# Revit family: WBW_VasteBeglazing 1 vak
name_source: partatom
category: Windows
revit_build: Autodesk Revit Architecture 2013 (Build: 20120221_2030(x64)
units: mm (PartAtom-declared; Revit-internal decimal feet)

## types (1)
- RT element vast beglaasd
    Aanzicht Kader 110mm = No
    Aanzicht Kader 68mm = Yes
    Aanzicht Kader 78mm = No
    Aanzicht Kader 88mm = No
    Aanzicht Tussen Regel 110mm = No
    Aanzicht Tussen Regel 150mm = No
    Aanzicht Tussen Regel 200mm = No
    Aanzicht Tussen Regel 68mm = No
    Aanzicht Tussen Regel 78mm = Yes
    Aanzicht Tussen Regel 88mm = No
    Aanzicht Tussen Stijl 110mm = No
    Aanzicht Tussen Stijl 150mm = No
    Aanzicht Tussen Stijl 200mm = No
    Aanzicht Tussen Stijl 68mm = No
    Aanzicht Tussen Stijl 78mm = Yes
    Aanzicht Tussen Stijl 88mm = No
    AanzichtLijnDraai = Yes
    Aanzichtbreedte Kozijn Profielen_68_78_88_110_150mm = 68
    Aanzichtbreedte Raamvleugel Profielen _35_45_66mm = 35
    Aanzichtbreedte Tussen Regels _68_78_88_110_150_200mm = 78
    Aanzichtbreedte Tussen Stijlen _68_78_88_110_150_200mm = 78
    AanzichtlLijnVal = Yes
    Analytic Construction = <None>
    Assembly Code = B2020110
    B1 = 500 mm  [stored 1.64042 ft]
    Beslag Resume 03 = Handgreep A-line (niet afsluitbaar) artikel 276 177
    Beslag Resume 04 = Vaste Beglazing
    Beslag Resume 05 = Inbraakwerend volgens attest ALCOA SKG.0055.0292.07.NL (klasse 2)
    Brandwerend volgens: = -
    Brandwerend volgens:2 = Niet van toepassing_geselecteerd
    Brandwerendheid = No
    BreedteMaat_1 = 0 mm  [stored 0 ft]
    BreedteMaat_2 = 0 mm  [stored 0 ft]
    BreedteMaat_3 = 0 mm  [stored 0 ft]
    BreedteMaat_4 = 0 mm  [stored 0 ft]
    BreedteMaat_5 = 0 mm  [stored 0 ft]
    Default Sill Height = 800 mm
    Description = Kawneer RT 72 raamelement volgens productomschrijving:
    Description 2 = 'Standaard systeemomschrijving RT 72 standaard vlak
    Diepte Versterking Binnenzijde_30_55_75 = 75 mm  [stored 0.246063 ft]
    Diepte Versterking Buitenzijde_30_50_85 = 30 mm  [stored 0.0984252 ft]
    Dikte Stelkozijn = 27 mm  [stored 0.0885827 ft]
    Dikte Stelkozijn onderzijde = 27 mm  [stored 0.0885827 ft]
    DikteStelkozijnOnderzijde_SpelingPui_BuitenbladMWOnderzijde = 17 mm  [stored 0.0557743 ft]
    DikteStelkozijn_SpelingPui_BuitenbladMW = 17 mm  [stored 0.0557743 ft]
    Glasdikte (totaal) = 29 mm  [stored 0.0951444 ft]
    GlassType = Glass, Clear Glazing, Low E
    HalveSpouw = 90 mm  [stored 0.295276 ft]
    HalveSpouw_OffsetVkKozijn_Stelkozijn = 104 mm
    Height = 1800 mm  [stored 5.90551 ft]
    Hoogte Tussen regel 1 = 0 mm  [stored 0 ft]
    Hoogte Tussen regel 2 = 0 mm  [stored 0 ft]
    Hoogte Tussen regel 3 = 0 mm  [stored 0 ft]
    Hoogte Tussen regel 4 = 0 mm  [stored 0 ft]
    Hoogte Tussen regel 5 = 0 mm  [stored 0 ft]
    Keynote = 30.34
    Kleur Binnenzijde = Kawneer RAL 9010
    Kleur Binnenzijde Vleugel = Kawneer RAL 9010
    Kleur Buitenzijde = Kawneer RAL 9010
    Kleur Buitenzijde Vleugel = Kawneer RAL 9010
    Kleur H&S = NVT
    Model = NL-SfB naam
    NL-SfB-Code = 31.21.22
    Nen 5096 R.c. 2 = Yes
    OffsetVkKozijnVkStelkozijn = 14 mm  [stored 0.0459318 ft]
    Operation = IfcWindow
    RT 52 = No
    RT 62 = No
    RT 72 = Yes
    ScheduleType |RF| = WBC_W_F
    Speling Pui_ buitenblad MW = 10 mm  [stored 0.0328084 ft]
    Speling Pui_buitenblad MW Onderzijde = 10 mm  [stored 0.0328084 ft]
    Spouwdiepte = 180 mm  [stored 0.590551 ft]
    Type Comments = Vrij te parameteriseren Revit Model
    URL = http://www.kawneer.com
    Versterking Binnenzijde = Yes
    Versterking Buitenzijde = No
    Wall Closure = By host
    Width = 1000 mm  [stored 3.28084 ft]

note: [stored X ft] marks values corroborated as IEEE doubles in the binary element streams (Revit-internal decimal feet)

## geometry (parser evidence)
native form markers: Blend x14, Sweep x10
no freeform markers — native parametric forms only
